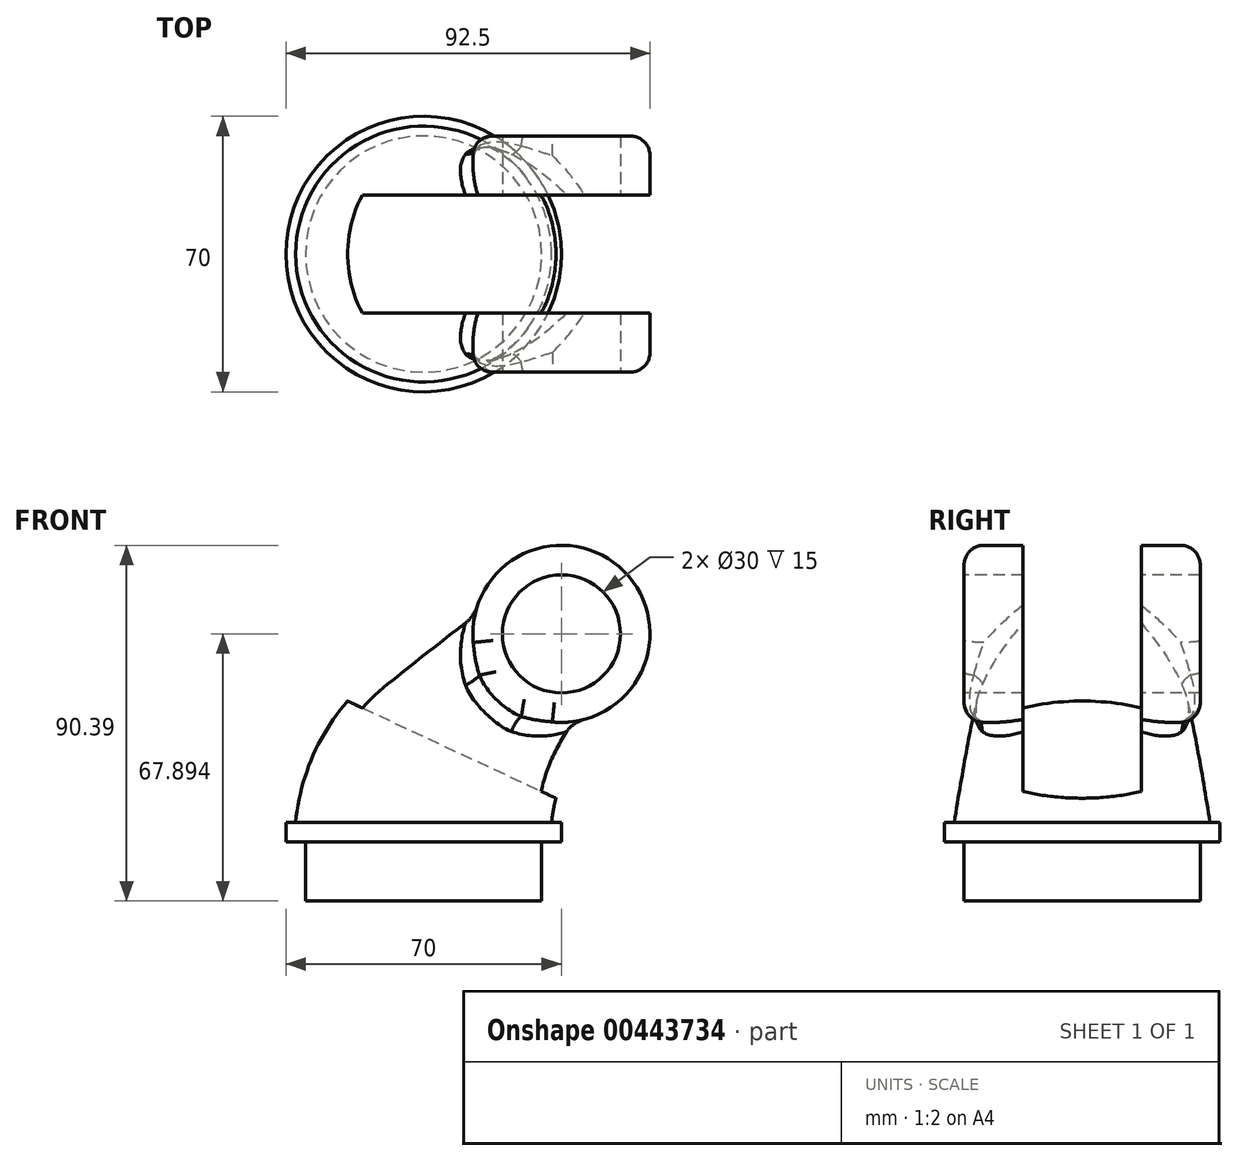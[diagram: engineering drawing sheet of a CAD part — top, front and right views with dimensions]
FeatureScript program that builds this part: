
annotation { "Feature Type Name" : "Feature", "Feature Type Description" : "" }
export const myFeature = defineFeature(function(context is Context, id is Id, definition is map)
    precondition{}
    {
        {
            var Q0;
            Q0=qCreatedBy(makeId("Top.planeOp"),FACE);
            var sketch = newSketch(context, id + "F0", { "sketchPlane" : qUnion([Q0])});
            skCircle(sketch, "E0", {"center": v(0, 0) * mm, "radius": 35 * mm});
            skSolve(sketch);
        }
        {
            var Q0;
            Q0 = qSketchRegion(id + "F0", true);
            extrude(context, id + "F1", {"entities" : qUnion([Q0]), "depth" : 5 * mm});
        }
        {
            var Q0;
            Q0=qCreatedBy(makeId("Front.planeOp"),FACE);
            var sketch = newSketch(context, id + "F2", { "sketchPlane" : qUnion([Q0])});
            skArc(sketch, "E1", {"start": v(17.6, 38.3) * mm, "mid": v(5.55, 23.37) * mm, "end": v(0, 5) * mm});
            skLineSegment(sketch, "E2", {"start": v(17.6, 38.3) * mm, "end": v(35, 52.9) * mm});
            skSolve(sketch);
        }
        {
            var Q0;
            Q0=sQuery(id+"F2.wireOp",EDGE,"E2");
            var Q1;
            Q1=sQuery(id+"F2.wireOp",VERTEX,"E2.end");
            cPlane(context, id + "F3", {"entities" : qUnion([Q0, Q1]), "cplaneType" : CPlaneType.LINE_POINT, "offset" : 25 * mm, "width" : 150 * mm, "height" : 150 * mm});
        }
        {
            var Q0;
            Q0=qCreatedBy(id+"F3.planeOp",FACE);
            var sketch = newSketch(context, id + "F4", { "sketchPlane" : qUnion([Q0])});
            skCircle(sketch, "E3", {"center": v(0, 18.02) * mm, "radius": 22.5 * mm});
            skSolve(sketch);
        }
        {
            var Q0;
            Q0=makeQuery(id+"F1.opExtrude","CAP_FACE",FACE,{"disambiguationData":[OSD([sQuery(id+"F0.wireOp",EDGE,"E0")])],"isStart":false});
            var sketch = newSketch(context, id + "F5", { "sketchPlane" : qUnion([Q0])});
            skCircle(sketch, "E4", {"center": v(0, 0) * mm, "radius": 32.5 * mm});
            skSolve(sketch);
        }
        {
            var Q0;
            Q0=qCreatedBy(makeId("Front.planeOp"),FACE);
            var sketch = newSketch(context, id + "F6", { "sketchPlane" : qUnion([Q0])});
            skArc(sketch, "E5", {"start": v(-13.25, 41.78) * mm, "mid": v(-26.5, 25.3) * mm, "end": v(-32.5, 5) * mm});
            skLineSegment(sketch, "E6", {"start": v(-13.25, 41.78) * mm, "end": v(20.54, 70.13) * mm});
            skSolve(sketch);
        }
        {
            var Q0;
            Q0=qCreatedBy(makeId("Front.planeOp"),FACE);
            var sketch = newSketch(context, id + "F7", { "sketchPlane" : qUnion([Q0])});
            skArc(sketch, "E7", {"start": v(48.46, 34.82) * mm, "mid": v(37.6, 21.45) * mm, "end": v(32.5, 5) * mm});
            skLineSegment(sketch, "E8", {"start": v(48.46, 34.82) * mm, "end": v(49.46, 35.66) * mm});
            skSolve(sketch);
        }
        {
            var Q1;
            Q1=makeQuery(id+"F5.imprint","IMPRINT",FACE,{"disambiguationData":[TD([[makeQuery(id+"F5.imprint","IMPRINT",EDGE,{"derivedFrom":sQuery(id+"F5.wireOp",EDGE,"E4")}),1.0]])]});
            var Q2;
            Q2=makeQuery(id+"F4.imprint","IMPRINT",FACE,{"disambiguationData":[TD([[makeQuery(id+"F4.imprint","IMPRINT",EDGE,{"derivedFrom":sQuery(id+"F4.wireOp",EDGE,"E3")}),1.0]])]});
            var Q3;
            Q3 = qConstructionFilter(qBodyType(qCreatedBy(id + "F7" ,EDGE), BodyType.WIRE), ConstructionObject.NO);
            var Q4;
            Q4 = qConstructionFilter(qBodyType(qCreatedBy(id + "F6" ,EDGE), BodyType.WIRE), ConstructionObject.NO);
            loft(context, id + "F8", {"operationType" : NewBodyOperationType.ADD, "addGuides" : true, "sheetProfilesArray" : [{ "sheetProfileEntities" : qUnion([Q1]) }, { "sheetProfileEntities" : qUnion([Q2]) }], "guidesArray" : [{ "guideEntities" : qUnion([Q3]), "guideDerivativeType" : LoftGuideDerivativeType.DEFAULT, "guideDerivativeMagnitude" : 1 }, { "guideEntities" : qUnion([Q4]), "guideDerivativeType" : LoftGuideDerivativeType.DEFAULT, "guideDerivativeMagnitude" : 1 }]});
        }
        {
            var Q0;
            Q0=qCreatedBy(makeId("Front.planeOp"),FACE);
            var sketch = newSketch(context, id + "F9", { "sketchPlane" : qUnion([Q0])});
            skCircle(sketch, "E9", {"center": v(35, 52.9) * mm, "radius": 22.5 * mm});
            skSolve(sketch);
        }
        {
            var Q0;
            Q0 = qSketchRegion(id + "F9", true);
            extrude(context, id + "F10", {"entities" : qUnion([Q0]), "operationType" : NewBodyOperationType.ADD, "endBound" : BoundingType.SYMMETRIC, "depth" : 60 * mm});
        }
        {
            var Q0;
            Q0=makeQuery(id+"F10.boolean.opBoolean","INTERSECT",EDGE,{"disambiguationData":[OD(0.0)],"derivedFrom":[makeQuery(id+"F8.opLoft","SWEPT_FACE",FACE,{"disambiguationData":[OSD([sQuery(id+"F4.wireOp",EDGE,"E3"),sQuery(id+"F5.wireOp",EDGE,"E4"),sQuery(id+"F6.wireOp",VERTEX,"E6.start"),sQuery(id+"F6.wireOp",EDGE,"E5"),sQuery(id+"F6.wireOp",EDGE,"E6"),sQuery(id+"F7.wireOp",VERTEX,"E8.start"),sQuery(id+"F7.wireOp",EDGE,"E7"),sQuery(id+"F7.wireOp",EDGE,"E8")])]}),makeQuery(id+"F10.opExtrude","SWEPT_FACE",FACE,{"disambiguationData":[OSD([sQuery(id+"F9.wireOp",EDGE,"E9")])]})]});
            var Q1;
            Q1=makeQuery(id+"F10.boolean.opBoolean","INTERSECT",EDGE,{"disambiguationData":[OD(1.0)],"derivedFrom":[makeQuery(id+"F8.opLoft","SWEPT_FACE",FACE,{"disambiguationData":[OSD([sQuery(id+"F4.wireOp",EDGE,"E3"),sQuery(id+"F5.wireOp",EDGE,"E4"),sQuery(id+"F6.wireOp",VERTEX,"E6.start"),sQuery(id+"F6.wireOp",EDGE,"E5"),sQuery(id+"F6.wireOp",EDGE,"E6"),sQuery(id+"F7.wireOp",VERTEX,"E8.start"),sQuery(id+"F7.wireOp",EDGE,"E7"),sQuery(id+"F7.wireOp",EDGE,"E8")])]}),makeQuery(id+"F10.opExtrude","SWEPT_FACE",FACE,{"disambiguationData":[OSD([sQuery(id+"F9.wireOp",EDGE,"E9")])]})]});
            fillet(context, id + "F11", {"entities" : qUnion([Q0, Q1]), "radius" : 5 * mm, "tangentPropagation" : true, "allowEdgeOverflow" : false});
        }
        {
            var Q0;
            Q0=makeQuery(id+"F10.opExtrude","CAP_FACE",FACE,{"disambiguationData":[OSD([sQuery(id+"F9.wireOp",EDGE,"E9")])],"isStart":false});
            var Q1;
            Q1=makeQuery(id+"F10.opExtrude","CAP_FACE",FACE,{"disambiguationData":[OSD([sQuery(id+"F9.wireOp",EDGE,"E9")])],"isStart":true});
            fillet(context, id + "F12", {"entities" : qUnion([Q0, Q1]), "radius" : 5 * mm, "tangentPropagation" : true, "allowEdgeOverflow" : false});
        }
        {
            var Q0;
            Q0=makeQuery(id+"F10.opExtrude","CAP_FACE",FACE,{"disambiguationData":[OSD([sQuery(id+"F9.wireOp",EDGE,"E9")])],"isStart":false});
            var sketch = newSketch(context, id + "F13", { "sketchPlane" : qUnion([Q0])});
            skCircle(sketch, "E10", {"center": v(35, 52.9) * mm, "radius": 15 * mm});
            skSolve(sketch);
        }
        {
            var Q0;
            Q0 = qSketchRegion(id + "F13", true);
            extrude(context, id + "F14", {"entities" : qUnion([Q0]), "operationType" : NewBodyOperationType.REMOVE, "endBound" : BoundingType.THROUGH_ALL, "oppositeDirection" : true, "depth" : 25 * mm});
        }
        {
            var Q0;
            Q0=qCreatedBy(makeId("Front.planeOp"),FACE);
            var sketch = newSketch(context, id + "F15", { "sketchPlane" : qUnion([Q0])});
            skLineSegment(sketch, "E11", {"start": v(-104.76, 75.66) * mm, "end": v(57.5, 0) * mm});
            skLineSegment(sketch, "E12", {"start": v(57.5, 75.66) * mm, "end": v(57.5, 0) * mm});
            skLineSegment(sketch, "E13", {"start": v(-104.76, 75.66) * mm, "end": v(57.5, 75.66) * mm});
            skSolve(sketch);
        }
        {
            var Q0;
            Q0 = qSketchRegion(id + "F15", true);
            extrude(context, id + "F16", {"entities" : qUnion([Q0]), "operationType" : NewBodyOperationType.REMOVE, "endBound" : BoundingType.SYMMETRIC, "oppositeDirection" : true, "depth" : 30 * mm});
        }
        {
            var Q0;
            Q0=qCreatedBy(makeId("Front.planeOp"),FACE);
            var sketch = newSketch(context, id + "F17", { "sketchPlane" : qUnion([Q0])});
            skLineSegment(sketch, "E14.bottom", {"start": v(0, 0) * mm, "end": v(-30, 0) * mm});
            skLineSegment(sketch, "E14.top", {"start": v(0, -15) * mm, "end": v(-30, -15) * mm});
            skLineSegment(sketch, "E14.left", {"start": v(0, 0) * mm, "end": v(0, -15) * mm});
            skLineSegment(sketch, "E14.right", {"start": v(-30, 0) * mm, "end": v(-30, -15) * mm});
            skSolve(sketch);
        }
        {
            var Q0;
            Q0 = qSketchRegion(id + "F17", true);
            var Q1;
            Q1=sQuery(id+"F17.wireOp",EDGE,"E14.left");
            revolve(context, id + "F18", {"operationType" : NewBodyOperationType.ADD, "entities" : qUnion([Q0]), "axis" : qUnion([Q1]), "revolveType" : RevolveType.FULL});
        }
    });
